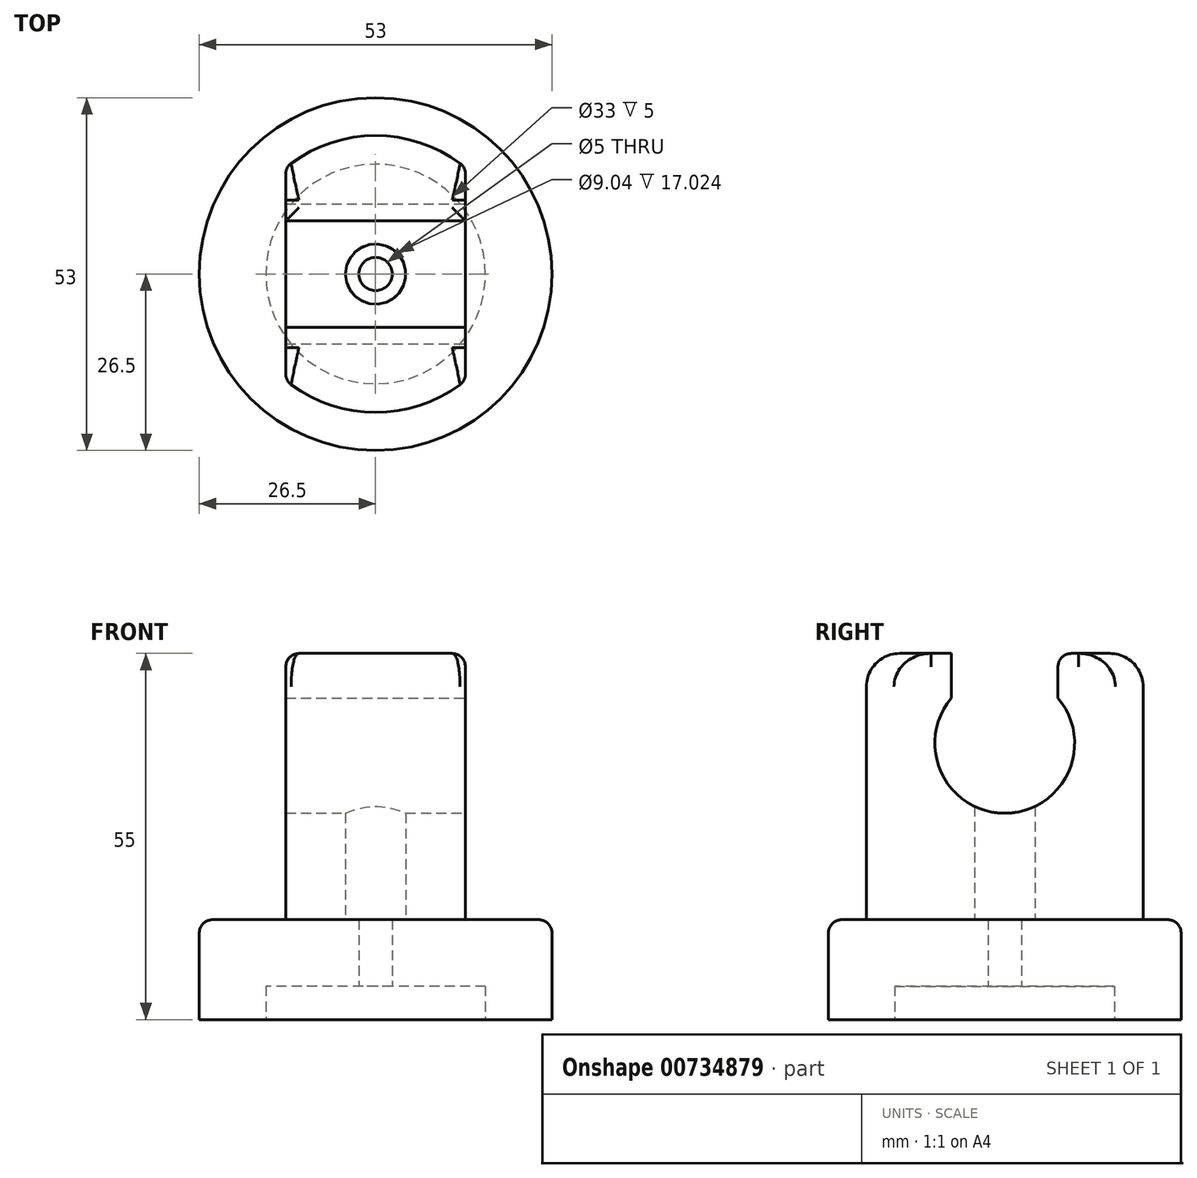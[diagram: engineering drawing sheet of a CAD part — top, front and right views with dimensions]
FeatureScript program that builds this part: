
annotation { "Feature Type Name" : "Feature", "Feature Type Description" : "" }
export const myFeature = defineFeature(function(context is Context, id is Id, definition is map)
    precondition{}
    {
        {
            var Q0;
            Q0=qCreatedBy(makeId("Top.planeOp"),FACE);
            var sketch = newSketch(context, id + "F0", { "sketchPlane" : qUnion([Q0])});
            skCircle(sketch, "E0", {"center": v(0, 0) * mm, "radius": 26.5 * mm});
            skLineSegment(sketch, "E1.bottom", {"start": v(-16.5, -13.5) * mm, "end": v(16.5, -13.5) * mm});
            skLineSegment(sketch, "E1.top", {"start": v(-16.5, 13.5) * mm, "end": v(16.5, 13.5) * mm});
            skLineSegment(sketch, "E1.left", {"start": v(-16.5, -13.5) * mm, "end": v(-16.5, 13.5) * mm});
            skLineSegment(sketch, "E1.right", {"start": v(16.5, -13.5) * mm, "end": v(16.5, 13.5) * mm});
            skArc(sketch, "E2", {"start": v(-16.5, 13.5) * mm, "mid": v(-21.13, 0) * mm, "end": v(-16.5, -13.5) * mm});
            skArc(sketch, "E3", {"start": v(16.5, -13.5) * mm, "mid": v(21.13, 0) * mm, "end": v(16.5, 13.5) * mm});
            skCircle(sketch, "E4", {"center": v(0, 0) * mm, "radius": 4.5 * mm});
            skCircle(sketch, "E5", {"center": v(0, 0) * mm, "radius": 2.5 * mm});
            skSolve(sketch);
        }
        {
            var Q0;
            Q0=makeQuery(id+"F0.imprint","IMPRINT",FACE,{"disambiguationData":[TD([[makeQuery(id+"F0.imprint","IMPRINT",EDGE,{"derivedFrom":sQuery(id+"F0.wireOp",EDGE,"E1.left")}),1.0]])]});
            var Q1;
            Q1=makeQuery(id+"F0.imprint","IMPRINT",FACE,{"disambiguationData":[TD([[makeQuery(id+"F0.imprint","IMPRINT",EDGE,{"derivedFrom":sQuery(id+"F0.wireOp",EDGE,"E1.right")}),-1.0]])]});
            var Q2;
            Q2=makeQuery(id+"F0.imprint","IMPRINT",FACE,{"disambiguationData":[TD([[makeQuery(id+"F0.imprint","IMPRINT",EDGE,{"derivedFrom":sQuery(id+"F0.wireOp",EDGE,"E0")}),1.0]])]});
            var Q3;
            Q3=makeQuery(id+"F0.imprint","IMPRINT",FACE,{"disambiguationData":[TD([[makeQuery(id+"F0.imprint","IMPRINT",EDGE,{"derivedFrom":sQuery(id+"F0.wireOp",EDGE,"E1.bottom")}),1.0]])]});
            var Q4;
            Q4=makeQuery(id+"F0.imprint","IMPRINT",FACE,{"disambiguationData":[TD([[makeQuery(id+"F0.imprint","IMPRINT",EDGE,{"derivedFrom":sQuery(id+"F0.wireOp",EDGE,"E4")}),1.0]])]});
            var Q5;
            Q5=makeQuery(id+"F0.imprint","IMPRINT",FACE,{"disambiguationData":[TD([[makeQuery(id+"F0.imprint","IMPRINT",EDGE,{"derivedFrom":sQuery(id+"F0.wireOp",EDGE,"E5")}),1.0]])]});
            var Q6;
            Q6 = qSketchRegion(id + "F7", true);
            extrude(context, id + "F1", {"entities" : qUnion([Q0, Q1, Q2, Q3, Q4, Q5, Q6]), "depth" : 15 * mm, "hasOffset" : true, "offsetDistance" : 25 * mm});
        }
        {
            var Q0;
            Q0=makeQuery(id+"F1.opExtrude","CAP_FACE",FACE,{"disambiguationData":[OSD([sQuery(id+"F0.wireOp",EDGE,"E0")])],"isStart":true});
            shell(context, id + "F2", {"entities" : qUnion([Q0]), "thickness" : 10 * mm});
        }
        {
            var Q0;
            Q0=makeQuery(id+"F1.opExtrude","CAP_FACE",FACE,{"disambiguationData":[OSD([sQuery(id+"F0.wireOp",EDGE,"E0")])],"isStart":true});
            var sketch = newSketch(context, id + "F3", { "sketchPlane" : qUnion([Q0])});
            skCircle(sketch, "E6", {"center": v(0, 0) * mm, "radius": 2.5 * mm});
            skSolve(sketch);
        }
        {
            var Q0;
            Q0=sQuery(id+"F3.wireOp",VERTEX,"E6.center");
            var Q1;
            Q1=makeQuery(id+"F1.opExtrude","SWEPT_BODY",BODY,{"disambiguationData":[OSD([sQuery(id+"F0.wireOp",EDGE,"E0")])]});
            hole(context, id + "F4", {"style" : HoleStyle.SIMPLE, "endStyle" : HoleEndStyle.THROUGH, "holeDiameter" : 5 * mm, "majorDiameter" : 5 * mm, "isTappedThrough" : true, "tappedDepth" : 12 * mm, "tapClearance" : 3, "locations" : qUnion([Q0]), "scope" : qUnion([Q1])});
        }
        {
            var Q0;
            Q0=makeQuery(id+"F1.opExtrude","CAP_FACE",FACE,{"disambiguationData":[OSD([sQuery(id+"F0.wireOp",EDGE,"E0")])],"isStart":false});
            var sketch = newSketch(context, id + "F5", { "sketchPlane" : qUnion([Q0])});
            skLineSegment(sketch, "E7.bottom", {"start": v(13.5, -16) * mm, "end": v(-13.5, -16) * mm});
            skLineSegment(sketch, "E7.top", {"start": v(13.5, 16) * mm, "end": v(-13.5, 16) * mm});
            skLineSegment(sketch, "E7.left", {"start": v(13.5, -16) * mm, "end": v(13.5, 16) * mm});
            skLineSegment(sketch, "E7.right", {"start": v(-13.5, -16) * mm, "end": v(-13.5, 16) * mm});
            skPoint(sketch, "E7.middle", {"position": v(0, 0) * mm});
            skArc(sketch, "E8", {"start": v(13.5, 16) * mm, "mid": v(0, 20.8) * mm, "end": v(-13.5, 16) * mm});
            skArc(sketch, "E9", {"start": v(-13.5, -16) * mm, "mid": v(0, -20.8) * mm, "end": v(13.5, -16) * mm});
            skCircle(sketch, "E10", {"center": v(0, 0) * mm, "radius": 4.52 * mm});
            skSolve(sketch);
        }
        {
            var Q0;
            Q0=makeQuery(id+"F5.imprint","IMPRINT",FACE,{"disambiguationData":[TD([[makeQuery(id+"F5.imprint","IMPRINT",EDGE,{"derivedFrom":sQuery(id+"F5.wireOp",EDGE,"E7.bottom")}),-1.0]])]});
            var Q1;
            Q1=makeQuery(id+"F5.imprint","IMPRINT",FACE,{"disambiguationData":[TD([[makeQuery(id+"F5.imprint","IMPRINT",EDGE,{"derivedFrom":sQuery(id+"F5.wireOp",EDGE,"E7.top")}),-1.0]])]});
            var Q2;
            Q2=makeQuery(id+"F5.imprint","IMPRINT",FACE,{"disambiguationData":[TD([[makeQuery(id+"F5.imprint","IMPRINT",EDGE,{"derivedFrom":sQuery(id+"F5.wireOp",EDGE,"E7.bottom")}),1.0]])]});
            extrude(context, id + "F6", {"entities" : qUnion([Q0, Q1, Q2]), "operationType" : NewBodyOperationType.ADD, "depth" : 40 * mm, "offsetDistance" : 25 * mm});
        }
        {
            var Q0;
            Q0=makeQuery(id+"F6.opExtrude","SWEPT_FACE",FACE,{"disambiguationData":[OSD([sQuery(id+"F5.wireOp",EDGE,"E7.left")])]});
            var sketch = newSketch(context, id + "F7", { "sketchPlane" : qUnion([Q0])});
            skCircle(sketch, "E11", {"center": v(0, 41.5) * mm, "radius": 10.5 * mm});
            skLineSegment(sketch, "E12.bottom", {"start": v(-8, 55) * mm, "end": v(8, 55) * mm});
            skLineSegment(sketch, "E12.top", {"start": v(-8, 48.3) * mm, "end": v(8, 48.3) * mm});
            skLineSegment(sketch, "E12.left", {"start": v(-8, 55) * mm, "end": v(-8, 48.3) * mm});
            skLineSegment(sketch, "E12.right", {"start": v(8, 55) * mm, "end": v(8, 48.3) * mm});
            skSolve(sketch);
        }
        {
            var Q0;
            {var subQ0=sQuery(id+"F7.wireOp",EDGE,"E12.top");Q0=makeQuery(id+"F7.imprint","IMPRINT",FACE,{"disambiguationData":[TD([[makeQuery(id+"F7.imprint","IMPRINT",EDGE,{"derivedFrom":subQ0}),-1.0]])]});}
            var Q1;
            {var subQ0=sQuery(id+"F7.wireOp",EDGE,"E12.top");Q1=makeQuery(id+"F7.imprint","IMPRINT",FACE,{"disambiguationData":[TD([[makeQuery(id+"F7.imprint","IMPRINT",EDGE,{"derivedFrom":subQ0}),1.0]])]});}
            var Q2;
            Q2=makeQuery(id+"F7.imprint","IMPRINT",FACE,{"disambiguationData":[TD([[makeQuery(id+"F7.imprint","IMPRINT",EDGE,{"derivedFrom":sQuery(id+"F7.wireOp",EDGE,"E12.bottom")}),-1.0]])]});
            extrude(context, id + "F8", {"entities" : qUnion([Q0, Q1, Q2]), "operationType" : NewBodyOperationType.REMOVE, "oppositeDirection" : true, "depth" : 27 * mm, "offsetDistance" : 25 * mm});
        }
        {
            var Q0;
            Q0=makeQuery(id+"F6.opExtrude","CAP_EDGE",EDGE,{"disambiguationData":[OSD([sQuery(id+"F5.wireOp",EDGE,"E9")])],"isStart":false});
            var Q1;
            Q1=makeQuery(id+"F6.opExtrude","CAP_EDGE",EDGE,{"disambiguationData":[OSD([sQuery(id+"F5.wireOp",EDGE,"E8")])],"isStart":false});
            fillet(context, id + "F9", {"entities" : qUnion([Q0, Q1]), "radius" : 5 * mm, "tangentPropagation" : true, "allowEdgeOverflow" : false});
        }
        {
            var Q0;
            Q0=makeQuery(id+"F8.boolean.opBoolean","COPY",EDGE,{"derivedFrom":makeQuery(id+"F8.opExtrude","SWEPT_EDGE",EDGE,{"disambiguationData":[OSD([sQuery(id+"F5.wireOp",EDGE,"E7.left"),sQuery(id+"F7.wireOp",EDGE,"E12.bottom"),sQuery(id+"F7.wireOp",EDGE,"E12.left")])]})});
            var Q1;
            Q1=makeQuery(id+"F8.boolean.opBoolean","COPY",EDGE,{"derivedFrom":makeQuery(id+"F8.opExtrude","SWEPT_EDGE",EDGE,{"disambiguationData":[OSD([sQuery(id+"F5.wireOp",EDGE,"E7.left"),sQuery(id+"F7.wireOp",EDGE,"E12.bottom"),sQuery(id+"F7.wireOp",EDGE,"E12.right")])]})});
            var Q2;
            Q2=makeQuery(id+"F8.boolean.opBoolean","COPY",EDGE,{"derivedFrom":makeQuery(id+"F8.opExtrude","CAP_EDGE",EDGE,{"disambiguationData":[OSD([sQuery(id+"F7.wireOp",EDGE,"E11")])],"isStart":true})});
            var Q3;
            Q3=makeQuery(id+"F8.boolean.opBoolean","COPY",EDGE,{"derivedFrom":makeQuery(id+"F8.opExtrude","CAP_EDGE",EDGE,{"disambiguationData":[OSD([sQuery(id+"F7.wireOp",EDGE,"E12.left")])],"isStart":true})});
            var Q4;
            Q4=makeQuery(id+"F8.boolean.opBoolean","COPY",EDGE,{"derivedFrom":makeQuery(id+"F8.opExtrude","CAP_EDGE",EDGE,{"disambiguationData":[OSD([sQuery(id+"F7.wireOp",EDGE,"E12.right")])],"isStart":true})});
            var Q5;
            Q5=makeQuery(id+"F8.boolean.opBoolean","COPY",EDGE,{"derivedFrom":makeQuery(id+"F8.opExtrude","CAP_EDGE",EDGE,{"disambiguationData":[OSD([sQuery(id+"F7.wireOp",EDGE,"E12.left")])],"isStart":false})});
            var Q6;
            Q6=makeQuery(id+"F8.boolean.opBoolean","COPY",EDGE,{"derivedFrom":makeQuery(id+"F8.opExtrude","CAP_EDGE",EDGE,{"disambiguationData":[OSD([sQuery(id+"F7.wireOp",EDGE,"E12.right")])],"isStart":false})});
            var Q7;
            Q7=makeQuery(id+"F8.boolean.opBoolean","COPY",EDGE,{"derivedFrom":makeQuery(id+"F8.opExtrude","CAP_EDGE",EDGE,{"disambiguationData":[OSD([sQuery(id+"F7.wireOp",EDGE,"E11")])],"isStart":false})});
            var Q8;
            Q8=makeQuery(id+"F1.opExtrude","CAP_EDGE",EDGE,{"disambiguationData":[OSD([sQuery(id+"F0.wireOp",EDGE,"E0")])],"isStart":false});
            var Q9;
            Q9=makeQuery(id+"F6.opExtrude","SWEPT_EDGE",EDGE,{"disambiguationData":[OSD([sQuery(id+"F5.wireOp",EDGE,"E7.top"),sQuery(id+"F5.wireOp",EDGE,"E7.left"),sQuery(id+"F5.wireOp",EDGE,"E8")])]});
            var Q10;
            Q10=makeQuery(id+"F6.opExtrude","SWEPT_EDGE",EDGE,{"disambiguationData":[OSD([sQuery(id+"F5.wireOp",EDGE,"E7.top"),sQuery(id+"F5.wireOp",EDGE,"E7.right"),sQuery(id+"F5.wireOp",EDGE,"E8")])]});
            var Q11;
            Q11=makeQuery(id+"F6.opExtrude","SWEPT_EDGE",EDGE,{"disambiguationData":[OSD([sQuery(id+"F5.wireOp",EDGE,"E7.bottom"),sQuery(id+"F5.wireOp",EDGE,"E7.right"),sQuery(id+"F5.wireOp",EDGE,"E9")])]});
            var Q12;
            Q12=makeQuery(id+"F6.opExtrude","SWEPT_EDGE",EDGE,{"disambiguationData":[OSD([sQuery(id+"F5.wireOp",EDGE,"E7.bottom"),sQuery(id+"F5.wireOp",EDGE,"E7.left"),sQuery(id+"F5.wireOp",EDGE,"E9")])]});
            fillet(context, id + "F10", {"entities" : qUnion([Q0, Q1, Q2, Q3, Q4, Q5, Q6, Q7, Q8, Q9, Q10, Q11, Q12]), "radius" : 2 * mm, "tangentPropagation" : true, "allowEdgeOverflow" : false});
        }
    });
